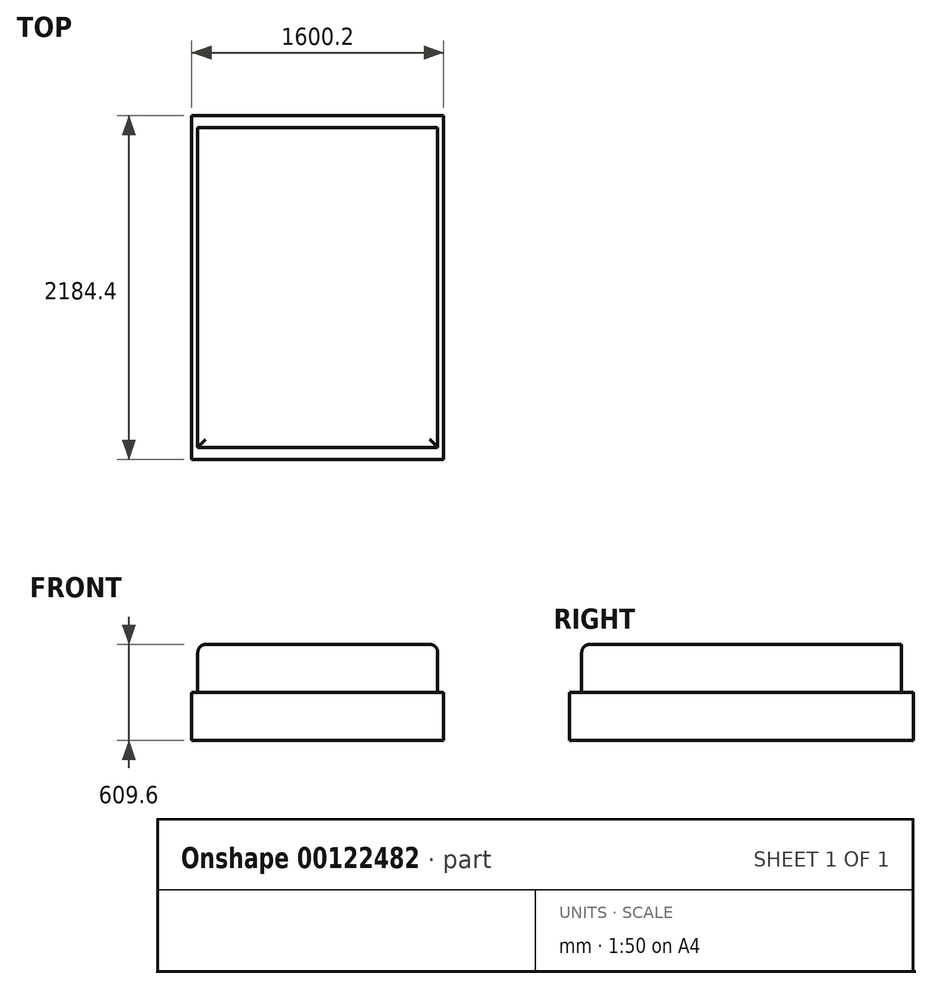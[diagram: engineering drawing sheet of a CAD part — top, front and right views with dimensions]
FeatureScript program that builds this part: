
annotation { "Feature Type Name" : "Feature", "Feature Type Description" : "" }
export const myFeature = defineFeature(function(context is Context, id is Id, definition is map)
    precondition{}
    {
        {
            var Q0;
            Q0=qCreatedBy(makeId("Top.planeOp"),FACE);
            var sketch = newSketch(context, id + "F0", { "sketchPlane" : qUnion([Q0])});
            skLineSegment(sketch, "E0.bottom", {"start": v(0, 0) * mm, "end": v(-1524, 0) * mm});
            skLineSegment(sketch, "E0.top", {"start": v(0, 2032) * mm, "end": v(-1524, 2032) * mm});
            skLineSegment(sketch, "E0.left", {"start": v(0, 0) * mm, "end": v(0, 2032) * mm});
            skLineSegment(sketch, "E0.right", {"start": v(-1524, 0) * mm, "end": v(-1524, 2032) * mm});
            skSolve(sketch);
        }
        {
            var Q0;
            Q0 = qSketchRegion(id + "F0", true);
            extrude(context, id + "F1", {"entities" : qUnion([Q0]), "depth" : 609.6 * mm});
        }
        {
            var Q0;
            Q0=makeQuery(id+"F1.opExtrude","CAP_EDGE",EDGE,{"disambiguationData":[OSD([sQuery(id+"F0.wireOp",EDGE,"E0.bottom")])],"isStart":false});
            var Q1;
            Q1=makeQuery(id+"F1.opExtrude","CAP_EDGE",EDGE,{"disambiguationData":[OSD([sQuery(id+"F0.wireOp",EDGE,"E0.right")])],"isStart":false});
            var Q2;
            Q2=makeQuery(id+"F1.opExtrude","CAP_EDGE",EDGE,{"disambiguationData":[OSD([sQuery(id+"F0.wireOp",EDGE,"E0.left")])],"isStart":false});
            fillet(context, id + "F2", {"entities" : qUnion([Q0, Q1, Q2]), "radius" : 50.8 * mm, "tangentPropagation" : true, "allowEdgeOverflow" : false});
        }
        {
            var Q0;
            Q0=qCreatedBy(makeId("Top.planeOp"),FACE);
            var sketch = newSketch(context, id + "F3", { "sketchPlane" : qUnion([Q0])});
            skLineSegment(sketch, "E1.bottom", {"start": v(38.1, -76.2) * mm, "end": v(-1562.1, -76.2) * mm});
            skLineSegment(sketch, "E1.top", {"start": v(38.1, 2108.2) * mm, "end": v(-1562.1, 2108.2) * mm});
            skLineSegment(sketch, "E1.left", {"start": v(38.1, -76.2) * mm, "end": v(38.1, 2108.2) * mm});
            skLineSegment(sketch, "E1.right", {"start": v(-1562.1, -76.2) * mm, "end": v(-1562.1, 2108.2) * mm});
            skSolve(sketch);
        }
        {
            var Q0;
            Q0 = qSketchRegion(id + "F3", true);
            extrude(context, id + "F4", {"entities" : qUnion([Q0]), "operationType" : NewBodyOperationType.ADD, "depth" : 304.8 * mm});
        }
    });
